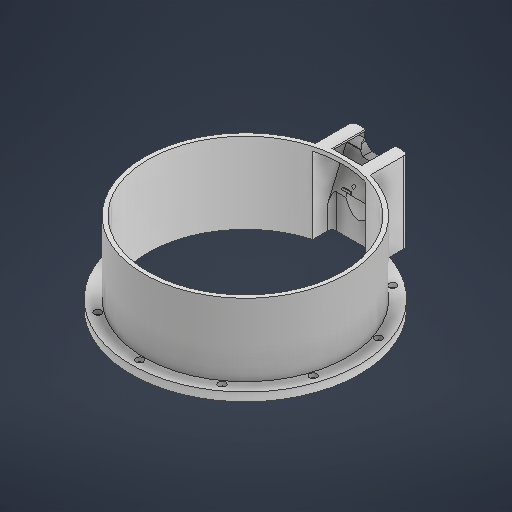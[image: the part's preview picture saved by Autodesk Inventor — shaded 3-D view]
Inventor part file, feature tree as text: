
AUTODESK INVENTOR PART (.ipt)
format: ipt  version: 2025 (Build 290162000, 162)  size: 569,344 bytes
history: native  units: in
note: dims shown in document units (in); Inventor stores cm internally (conversion verified against a paired STEP export)
features: extrude x20, sketch x18, other x3, plane x3, chamfer x3, fillet x2
ambient origin geometry x8: Origin, YZ Plane, XZ Plane, XY Plane, X Axis, Y Axis, Z Axis, Center Point
bodies: Body1 (feature_tree)
feature tree (49):
  other  "Cylinder.ipt"
  extrude  "Extrusion1"  Depth=0.3937in
  extrude  "Extrusion2"  Depth=0.3937in TaperAngle=0.0deg
  sketch  "Sketch3"  dims[d7=11.2205in d8=10.6299in]
  extrude  "Extrusion3"  Depth=10.6299in
  extrude  "Extrusion5"  Depth=0.1969in TaperAngle=0.0deg
  sketch  "Sketch6"  dims[d24=0.1969in d25=0.0in d31=0.0in d32=0.0in]
  extrude  "Extrusion6"  Depth=0.2953in
  extrude  "Extrusion7"  TaperAngle=0.0deg  [1 undecoded]
  extrude  "Extrusion8"  Depth=9.8425in
  plane  "Work Plane1"
  extrude  "Extrusion9"  Depth=10.6299in
  extrude  "Extrusion21"  Depth=0.0787in
  sketch  "Sketch19"  dims[d107=2.2047in d108=0.0in d113=2.5591in]
  extrude  "Extrusion34"  Depth=2.5591in
  extrude  "Extrusion43"  Depth=0.0591in
  extrude  "Extrusion44"  Depth=0.0787in
  extrude  "Extrusion45"  Depth=0.0787in
  chamfer  "Chamfer8"  Distance=1.1614in
  sketch  "Sketch31"  dims[d164=1.5298in d165=0.0787in]
  extrude  "Extrusion46"  Depth=0.2165in
  extrude  "Extrusion47"  Depth=3.937in TaperAngle=360.0deg
  plane  "Work Plane2"
  extrude  "Extrusion48"  Depth=0.1969in
  plane  "Work Plane3"
  sketch  "Sketch33"  dims[d167=90.0deg d173=1.1614in d174=0.0in]
  extrude  "Extrusion49"  Depth=0.1969in
  extrude  "Extrusion50"  Depth=0.1969in
  extrude  "Extrusion51"  Depth=0.1969in
  extrude  "Extrusion52"  Depth=0.1969in
  chamfer  "Chamfer9"  Distance=2.7608in
  chamfer  "Chamfer10"  Distance=3.5433in
  fillet  "Fillet19"  Radius=3.1693in
  fillet  "Fillet21"  Radius=3.3661in
  other  "Solid12::Cylinder.ipt"
  other  "TaggingFeature1"
  sketch  "Sketch1"  dims[d0=0.3937in d2=10.2362in]
  sketch  "Sketch2"  dims[d3=0.0in d4=0.0in d5=0.3937in d6=0.0in]
  sketch  "Sketch5"  dims[d17=10.6299in d18=0.2953in]
  sketch  "Sketch7"  dims[d33=2.1654in d34=0.0in d35=9.8425in]
  sketch  "Sketch9"  dims[d36=10.6299in d46=9.065in]
  sketch  "Sketch14"  dims[d47=0.3937in d48=0.0in d88=0.0787in]
  sketch  "Sketch22"  dims[d117=0.0591in d120=0.5433in]
  sketch  "Sketch Circular Pattern3"  dims[d10=0.1969in d11=0.0in d15=0.1969in d16=0.0in]
  sketch  "Sketch30"  dims[d122=9.4488in d134=0.0787in]
  sketch  "Sketch32"  dims[d166=1.8325in]
  sketch  "Sketch34"  dims[d175=0.0787in d209=0.2165in]
  sketch  "Sketch35"  dims[d210=0.3425in d211=3.937in d213=360.0deg]
  sketch  "Sketch36"  dims[d217=10.4151in d218=9.065in d223=0.5433in d224=1.8228in d225=3.5433in d226=2.564in d227=2.7608in d228=3.5433in d233=3.1693in d234=1.5846in d235=0.0in d236=0.0in d237=3.3661in d238=0.3937in d239=0.0in d240=0.0in d241=0.9843in d242=3.1496in d243=0.0in d244=1.5748in d245=0.0787in d246=0.1598in d247=0.4331in d248=0.1575in d249=0.1575in d250=0.1575in d251=0.9331in d252=0.3937in d254=0.3937in d255=0.9331in d256=0.4331in d257=0.4331in d258=2.1654in d259=0.0in d260=0.1772in d261=0.0in d262=0.315in d263=0.1666in d265=1.5871in d266=0.0in d267=1.5748in d268=0.5315in d269=-3.5433in d270=1.378in d271=1.378in d272=9.7638in d273=0.0787in d274=0.0in d275=0.6412in d276=0.0in d277=1.378in d278=0.0787in d279=1.5787in d280=0.0in d281=0.0787in d282=0.8268in d283=0.3937in d284=0.0787in d285=0.3937in d286=0.0463in d287=0.3937in d288=0.0787in d289=0.3937in d290=0.0463in d291=0.0787in d292=0.0in d293=1.378in d294=0.2756in d295=0.3076in d296=45.0deg d297=0.2756in d298=0.3076in d299=45.0deg d300=0.1969in d305=0.1969in d143=0.0197in d144=0.0344in d145=0.0197in d146=0.0344in d153=0.0in d154=0.0in d155=0.0in d156=0.0in d201=0.0197in d202=0.0344in d203=0.0197in d204=0.0344in d215=0.0197in d216=0.0344in]
note: 1 required parameter value undecoded (feature->parameter linkage not recoverable at this tier; creation-order binding heuristic only, values carry confidence <= 0.55)
